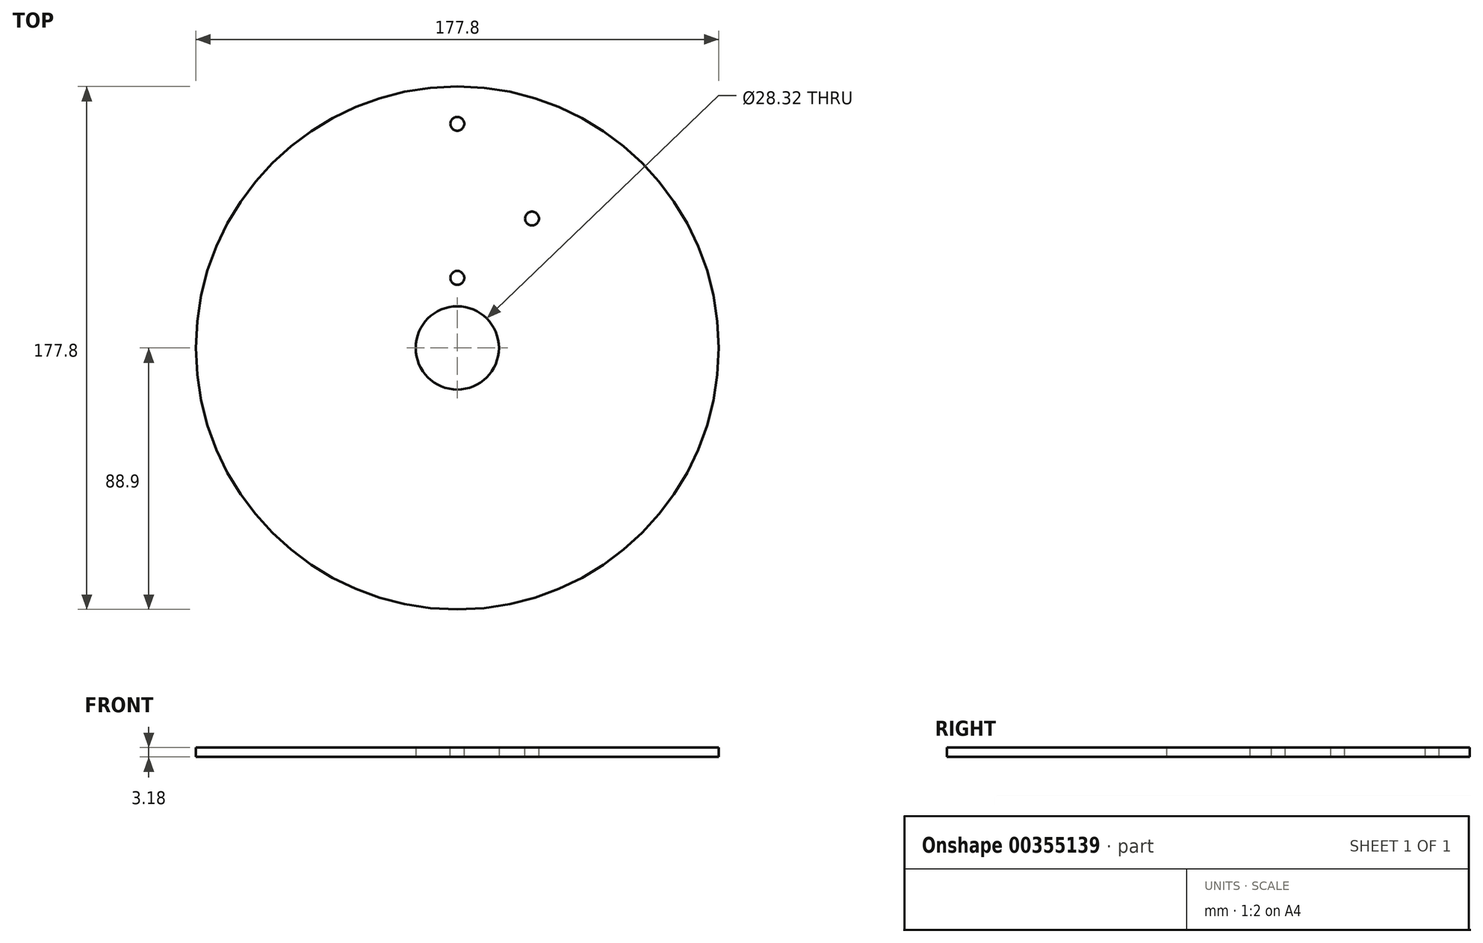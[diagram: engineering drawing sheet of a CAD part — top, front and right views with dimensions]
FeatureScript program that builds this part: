
annotation { "Feature Type Name" : "Feature", "Feature Type Description" : "" }
export const myFeature = defineFeature(function(context is Context, id is Id, definition is map)
    precondition{}
    {
        {
            var Q0;
            Q0=qCreatedBy(makeId("Top.planeOp"),FACE);
            var sketch = newSketch(context, id + "F0", { "sketchPlane" : qUnion([Q0])});
            skCircle(sketch, "E0", {"center": v(0, 0) * mm, "radius": 88.9 * mm});
            skCircle(sketch, "E1", {"center": v(0, 0) * mm, "radius": 14.16 * mm});
            skSolve(sketch);
        }
        {
            var Q0;
            Q0=makeQuery(id+"F0.imprint","IMPRINT",FACE,{"disambiguationData":[TD([[makeQuery(id+"F0.imprint","IMPRINT",EDGE,{"derivedFrom":sQuery(id+"F0.wireOp",EDGE,"E0")}),1.0]])]});
            extrude(context, id + "F1", {"entities" : qUnion([Q0]), "depth" : 3.17 * mm});
        }
        {
            var Q0;
            Q0=makeQuery(id+"F1.opExtrude","CAP_FACE",FACE,{"disambiguationData":[OSD([sQuery(id+"F0.wireOp",EDGE,"E0"),sQuery(id+"F0.wireOp",EDGE,"E1")])],"isStart":false});
            var sketch = newSketch(context, id + "F2", { "sketchPlane" : qUnion([Q0])});
            skCircle(sketch, "E2", {"center": v(0, 23.81) * mm, "radius": 2.36 * mm});
            skCircle(sketch, "E3", {"center": v(0, 76.2) * mm, "radius": 2.36 * mm});
            skCircle(sketch, "E4", {"center": v(25.4, 44) * mm, "radius": 2.36 * mm});
            skLineSegment(sketch, "E5", {"start": v(0, 0) * mm, "end": v(25.4, 44) * mm, "construction": true});
            skSolve(sketch);
        }
        {
            var Q0;
            Q0 = qSketchRegion(id + "F2", true);
            extrude(context, id + "F3", {"entities" : qUnion([Q0]), "operationType" : NewBodyOperationType.REMOVE, "endBound" : BoundingType.THROUGH_ALL, "oppositeDirection" : true, "depth" : 25.4 * mm});
        }
    });
